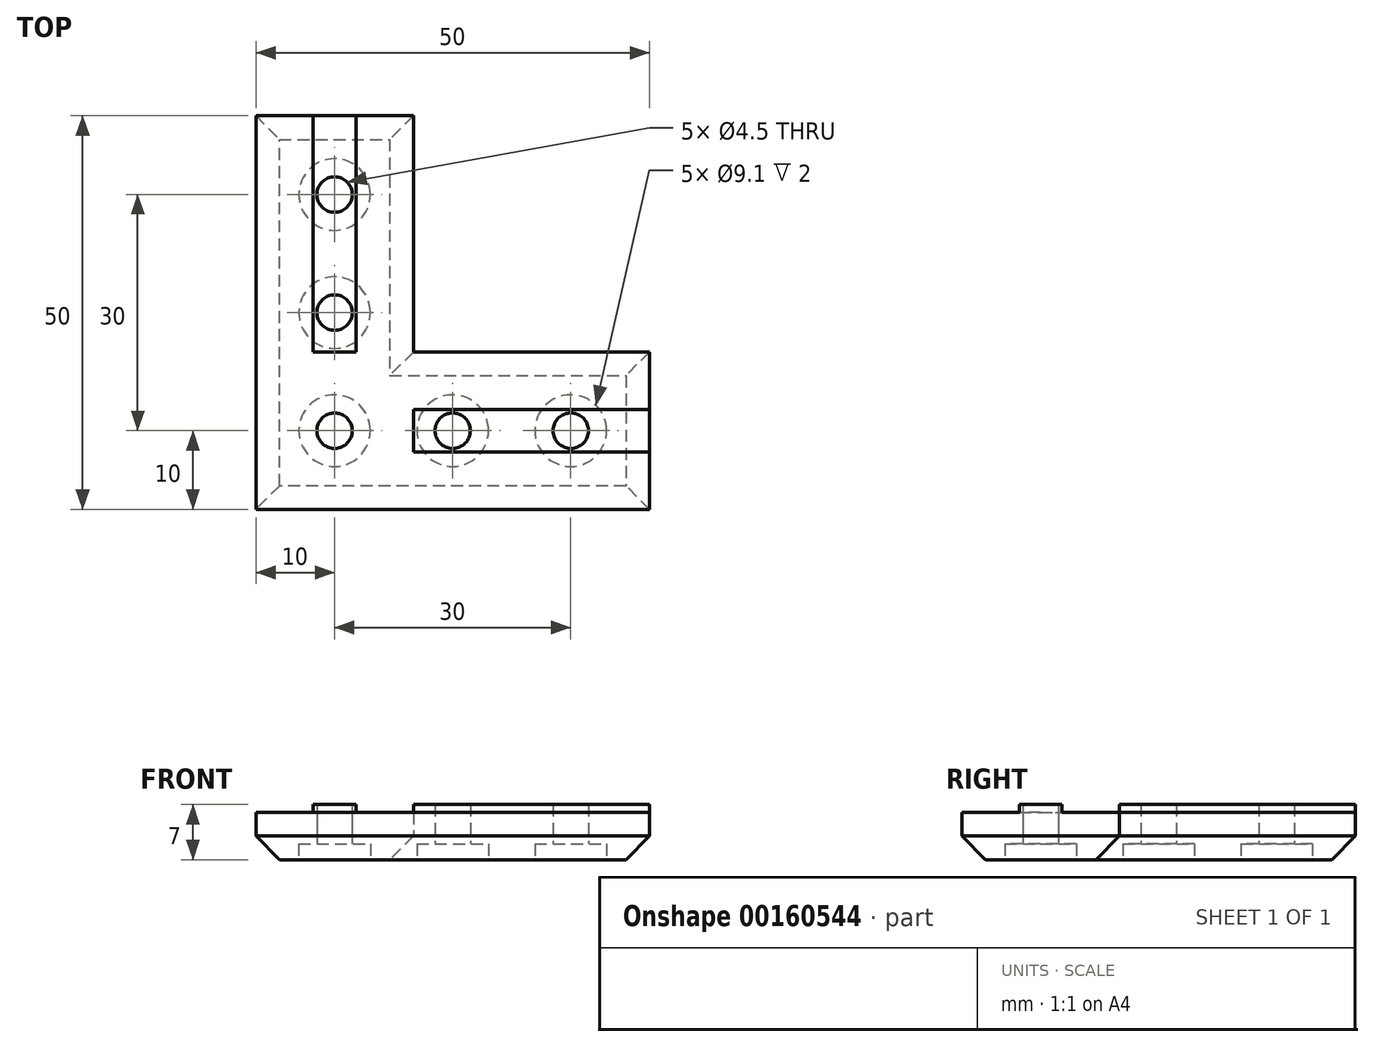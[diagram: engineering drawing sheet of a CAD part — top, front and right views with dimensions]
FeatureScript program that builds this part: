
annotation { "Feature Type Name" : "Feature", "Feature Type Description" : "" }
export const myFeature = defineFeature(function(context is Context, id is Id, definition is map)
    precondition{}
    {
        {
            var Q0;
            Q0=qCreatedBy(makeId("Top.planeOp"),FACE);
            var sketch = newSketch(context, id + "F0", { "sketchPlane" : qUnion([Q0])});
            skLineSegment(sketch, "E0", {"start": v(0, 0) * mm, "end": v(0, 50) * mm});
            skLineSegment(sketch, "E1", {"start": v(0, 50) * mm, "end": v(20, 50) * mm});
            skLineSegment(sketch, "E2", {"start": v(20, 50) * mm, "end": v(20, 20) * mm});
            skLineSegment(sketch, "E3", {"start": v(20, 20) * mm, "end": v(50, 20) * mm});
            skLineSegment(sketch, "E4", {"start": v(50, 20) * mm, "end": v(50, 0) * mm});
            skLineSegment(sketch, "E5", {"start": v(50, 0) * mm, "end": v(0, 0) * mm});
            skSolve(sketch);
        }
        {
            var Q0;
            Q0=qSketchRegion(id+"F0",true);
            extrude(context, id + "F1", {"entities" : qUnion([Q0]), "depth" : 6 * mm});
        }
        {
            var Q0;
            Q0=makeQuery(id+"F1.opExtrude","CAP_FACE",FACE,{"disambiguationData":[OSD([sQuery(id+"F0.wireOp",EDGE,"E0"),sQuery(id+"F0.wireOp",EDGE,"E1"),sQuery(id+"F0.wireOp",EDGE,"E2"),sQuery(id+"F0.wireOp",EDGE,"E3"),sQuery(id+"F0.wireOp",EDGE,"E4"),sQuery(id+"F0.wireOp",EDGE,"E5")])],"isStart":false});
            var sketch = newSketch(context, id + "F2", { "sketchPlane" : qUnion([Q0])});
            skLineSegment(sketch, "E6", {"start": v(7.3, 50) * mm, "end": v(12.71, 50) * mm});
            skLineSegment(sketch, "E7", {"start": v(12.71, 50) * mm, "end": v(12.71, 20) * mm});
            skLineSegment(sketch, "E8", {"start": v(12.71, 20) * mm, "end": v(10, 20) * mm});
            skPoint(sketch, "E8.endSnap0", {"position": v(10, 50) * mm});
            skLineSegment(sketch, "E9", {"start": v(10, 20) * mm, "end": v(7.3, 20) * mm});
            skLineSegment(sketch, "E10", {"start": v(7.3, 20) * mm, "end": v(7.3, 50) * mm});
            skLineSegment(sketch, "E11", {"start": v(50, 12.7) * mm, "end": v(50, 7.3) * mm});
            skLineSegment(sketch, "E12", {"start": v(50, 7.3) * mm, "end": v(20, 7.3) * mm});
            skLineSegment(sketch, "E13", {"start": v(20, 7.3) * mm, "end": v(20, 10) * mm});
            skPoint(sketch, "E13.endSnap0", {"position": v(50, 10) * mm});
            skLineSegment(sketch, "E14", {"start": v(20, 10) * mm, "end": v(20, 12.71) * mm});
            skLineSegment(sketch, "E15", {"start": v(20, 12.71) * mm, "end": v(50, 12.71) * mm});
            skSolve(sketch);
        }
        {
            var Q0;
            Q0=qSketchRegion(id+"F2",true);
            extrude(context, id + "F3", {"entities" : qUnion([Q0]), "operationType" : NewBodyOperationType.ADD, "flatOperationType" : FlatOperationType.REMOVE, "offsetDistance" : 25 * mm, "depth" : 1 * mm, "domain" : OperationDomain.MODEL});
        }
        {
            var Q0;
            Q0=makeQuery(id+"F1.opExtrude","CAP_FACE",FACE,{"disambiguationData":[OSD([sQuery(id+"F0.wireOp",EDGE,"E0"),sQuery(id+"F0.wireOp",EDGE,"E1"),sQuery(id+"F0.wireOp",EDGE,"E2"),sQuery(id+"F0.wireOp",EDGE,"E3"),sQuery(id+"F0.wireOp",EDGE,"E4"),sQuery(id+"F0.wireOp",EDGE,"E5")])],"isStart":true});
            var sketch = newSketch(context, id + "F4", { "sketchPlane" : qUnion([Q0])});
            skCircle(sketch, "E16", {"center": v(10, -10) * mm, "radius": 2.25 * mm});
            skCircle(sketch, "E17", {"center": v(40, -10) * mm, "radius": 2.25 * mm});
            skCircle(sketch, "E18", {"center": v(10, -40) * mm, "radius": 2.25 * mm});
            skCircle(sketch, "E19", {"center": v(25, -10) * mm, "radius": 2.25 * mm});
            skCircle(sketch, "E20", {"center": v(10, -25) * mm, "radius": 2.25 * mm});
            skSolve(sketch);
        }
        {
            var Q0;
            Q0 = qSketchRegion(id + "F4", true);
            extrude(context, id + "F5", {"entities" : qUnion([Q0]), "operationType" : NewBodyOperationType.REMOVE, "endBound" : BoundingType.THROUGH_ALL, "oppositeDirection" : true, "depth" : 25 * mm});
        }
        {
            var Q0;
            Q0=makeQuery(id+"F1.opExtrude","CAP_FACE",FACE,{"disambiguationData":[OSD([sQuery(id+"F0.wireOp",EDGE,"E0"),sQuery(id+"F0.wireOp",EDGE,"E1"),sQuery(id+"F0.wireOp",EDGE,"E2"),sQuery(id+"F0.wireOp",EDGE,"E3"),sQuery(id+"F0.wireOp",EDGE,"E4"),sQuery(id+"F0.wireOp",EDGE,"E5")])],"isStart":true});
            var sketch = newSketch(context, id + "F6", { "sketchPlane" : qUnion([Q0])});
            skCircle(sketch, "E21", {"center": v(10, -10) * mm, "radius": 4.55 * mm});
            skCircle(sketch, "E22", {"center": v(25, -10) * mm, "radius": 4.55 * mm});
            skCircle(sketch, "E23", {"center": v(40, -10) * mm, "radius": 4.55 * mm});
            skCircle(sketch, "E24", {"center": v(10, -25) * mm, "radius": 4.55 * mm});
            skCircle(sketch, "E25", {"center": v(10, -40) * mm, "radius": 4.55 * mm});
            skSolve(sketch);
        }
        {
            var Q0;
            Q0 = qSketchRegion(id + "F6", true);
            extrude(context, id + "F7", {"entities" : qUnion([Q0]), "operationType" : NewBodyOperationType.REMOVE, "oppositeDirection" : true, "depth" : 2 * mm});
        }
        {
            var Q0;
            Q0=makeQuery(id+"F1.opExtrude","CAP_EDGE",EDGE,{"disambiguationData":[OSD([sQuery(id+"F0.wireOp",EDGE,"E5")])],"isStart":true});
            var Q1;
            Q1=makeQuery(id+"F1.opExtrude","CAP_EDGE",EDGE,{"disambiguationData":[OSD([sQuery(id+"F0.wireOp",EDGE,"E0")])],"isStart":true});
            var Q2;
            Q2=makeQuery(id+"F1.opExtrude","CAP_EDGE",EDGE,{"disambiguationData":[OSD([sQuery(id+"F0.wireOp",EDGE,"E2")])],"isStart":true});
            var Q3;
            Q3=makeQuery(id+"F1.opExtrude","CAP_EDGE",EDGE,{"disambiguationData":[OSD([sQuery(id+"F0.wireOp",EDGE,"E3")])],"isStart":true});
            var Q4;
            Q4=makeQuery(id+"F1.opExtrude","CAP_EDGE",EDGE,{"disambiguationData":[OSD([sQuery(id+"F0.wireOp",EDGE,"E4")])],"isStart":true});
            var Q5;
            Q5=makeQuery(id+"F1.opExtrude","CAP_EDGE",EDGE,{"disambiguationData":[OSD([sQuery(id+"F0.wireOp",EDGE,"E1")])],"isStart":true});
            chamfer(context, id + "F8", {"entities" : qUnion([Q0, Q1, Q2, Q3, Q4, Q5]), "width" : 3 * mm, "tangentPropagation" : true});
        }
    });
